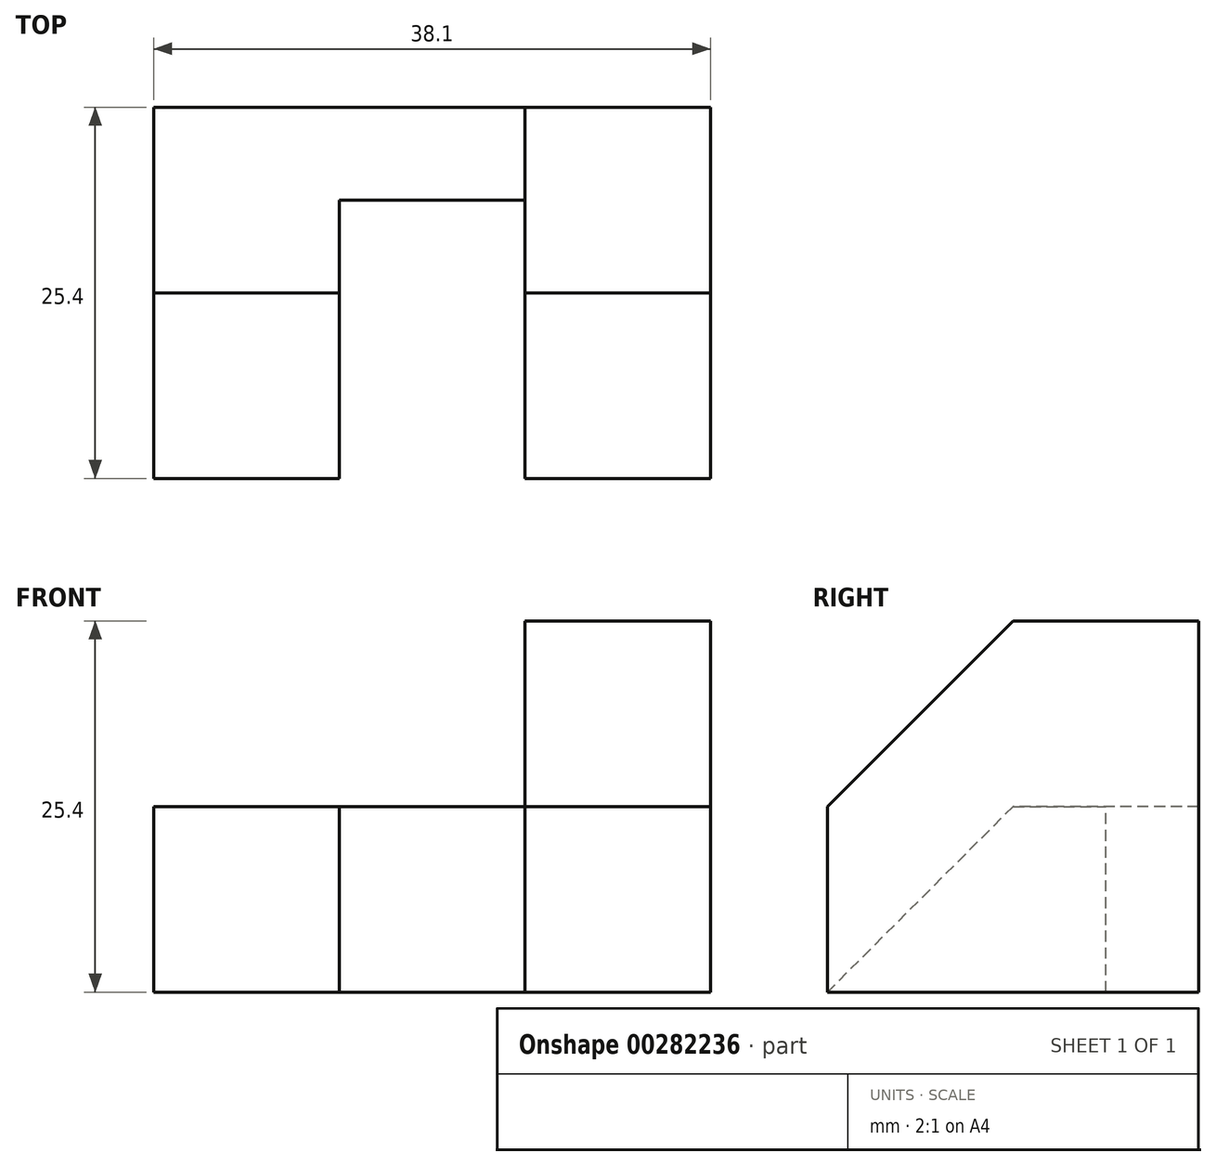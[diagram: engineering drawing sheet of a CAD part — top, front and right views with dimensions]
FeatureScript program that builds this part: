
annotation { "Feature Type Name" : "Feature", "Feature Type Description" : "" }
export const myFeature = defineFeature(function(context is Context, id is Id, definition is map)
    precondition{}
    {
        {
            var Q0;
            Q0=qCreatedBy(makeId("Right.planeOp"),FACE);
            var sketch = newSketch(context, id + "F0", { "sketchPlane" : qUnion([Q0])});
            skLineSegment(sketch, "E0.bottom", {"start": v(0, 0) * mm, "end": v(25.4, 0) * mm});
            skLineSegment(sketch, "E0.top", {"start": v(0, 25.4) * mm, "end": v(25.4, 25.4) * mm});
            skLineSegment(sketch, "E0.left", {"start": v(0, 0) * mm, "end": v(0, 25.4) * mm});
            skLineSegment(sketch, "E0.right", {"start": v(25.4, 0) * mm, "end": v(25.4, 25.4) * mm});
            skSolve(sketch);
        }
        {
            var Q0;
            Q0 = qSketchRegion(id + "F0", true);
            extrude(context, id + "F1", {"entities" : qUnion([Q0]), "depth" : 12.7 * mm});
        }
        {
            var Q0;
            Q0=makeQuery(id+"F1.opExtrude","CAP_FACE",FACE,{"disambiguationData":[OSD([sQuery(id+"F0.wireOp",EDGE,"E0.bottom"),sQuery(id+"F0.wireOp",EDGE,"E0.top"),sQuery(id+"F0.wireOp",EDGE,"E0.left"),sQuery(id+"F0.wireOp",EDGE,"E0.right")])],"isStart":false});
            var sketch = newSketch(context, id + "F2", { "sketchPlane" : qUnion([Q0])});
            skLineSegment(sketch, "E1", {"start": v(0, 25.4) * mm, "end": v(12.7, 25.4) * mm});
            skLineSegment(sketch, "E2", {"start": v(12.7, 25.4) * mm, "end": v(0, 12.7) * mm});
            skLineSegment(sketch, "E3", {"start": v(0, 12.7) * mm, "end": v(0, 25.4) * mm});
            skSolve(sketch);
        }
        {
            var Q0;
            Q0 = qSketchRegion(id + "F2", true);
            var Q1;
            Q1=makeQuery(id+"F2.imprint","IMPRINT",FACE,{"disambiguationData":[TD([[makeQuery(id+"F2.imprint","IMPRINT",EDGE,{"derivedFrom":sQuery(id+"F2.wireOp",EDGE,"E1")}),-1.0]])]});
            extrude(context, id + "F3", {"entities" : qUnion([Q0, Q1]), "operationType" : NewBodyOperationType.REMOVE, "oppositeDirection" : true, "depth" : 12.7 * mm});
        }
        {
            var Q0;
            Q0=makeQuery(id+"F1.opExtrude","CAP_FACE",FACE,{"disambiguationData":[OSD([sQuery(id+"F0.wireOp",EDGE,"E0.bottom"),sQuery(id+"F0.wireOp",EDGE,"E0.top"),sQuery(id+"F0.wireOp",EDGE,"E0.left"),sQuery(id+"F0.wireOp",EDGE,"E0.right")])],"isStart":true});
            var sketch = newSketch(context, id + "F4", { "sketchPlane" : qUnion([Q0])});
            skLineSegment(sketch, "E4.bottom", {"start": v(-25.4, 0) * mm, "end": v(-19.05, 0) * mm});
            skLineSegment(sketch, "E4.top", {"start": v(-25.4, 12.7) * mm, "end": v(-19.05, 12.7) * mm});
            skLineSegment(sketch, "E4.left", {"start": v(-25.4, 0) * mm, "end": v(-25.4, 12.7) * mm});
            skLineSegment(sketch, "E4.right", {"start": v(-19.05, 0) * mm, "end": v(-19.05, 12.7) * mm});
            skSolve(sketch);
        }
        {
            var Q0;
            Q0=makeQuery(id+"F4.imprint","IMPRINT",FACE,{"disambiguationData":[TD([[makeQuery(id+"F4.imprint","IMPRINT",EDGE,{"derivedFrom":sQuery(id+"F4.wireOp",EDGE,"E4.bottom")}),-1.0]])]});
            extrude(context, id + "F5", {"entities" : qUnion([Q0]), "operationType" : NewBodyOperationType.ADD, "depth" : 25.4 * mm});
        }
        {
            var Q0;
            Q0=makeQuery(id+"F5.opExtrude","SWEPT_FACE",FACE,{"disambiguationData":[OSD([sQuery(id+"F4.wireOp",EDGE,"E4.right")])]});
            var sketch = newSketch(context, id + "F6", { "sketchPlane" : qUnion([Q0])});
            skLineSegment(sketch, "E5.bottom", {"start": v(-25.4, 0) * mm, "end": v(-12.7, 0) * mm});
            skLineSegment(sketch, "E5.top", {"start": v(-25.4, 12.7) * mm, "end": v(-12.7, 12.7) * mm});
            skLineSegment(sketch, "E5.left", {"start": v(-25.4, 0) * mm, "end": v(-25.4, 12.7) * mm});
            skLineSegment(sketch, "E5.right", {"start": v(-12.7, 0) * mm, "end": v(-12.7, 12.7) * mm});
            skSolve(sketch);
        }
        {
            var Q0;
            Q0 = qSketchRegion(id + "F6", true);
            extrude(context, id + "F7", {"entities" : qUnion([Q0]), "operationType" : NewBodyOperationType.ADD, "depth" : 19.05 * mm});
        }
        {
            var Q0;
            Q0=makeQuery(id+"F7.opExtrude","SWEPT_FACE",FACE,{"disambiguationData":[OSD([sQuery(id+"F6.wireOp",EDGE,"E5.right")])]});
            var sketch = newSketch(context, id + "F8", { "sketchPlane" : qUnion([Q0])});
            skLineSegment(sketch, "E6", {"start": v(0, 0) * mm, "end": v(0, 12.7) * mm});
            skLineSegment(sketch, "E7", {"start": v(0, 12.7) * mm, "end": v(12.7, 12.7) * mm});
            skLineSegment(sketch, "E8", {"start": v(12.7, 12.7) * mm, "end": v(0, 0) * mm});
            skSolve(sketch);
        }
        {
            var Q0;
            Q0=makeQuery(id+"F8.imprint","IMPRINT",FACE,{"disambiguationData":[TD([[makeQuery(id+"F8.imprint","IMPRINT",EDGE,{"derivedFrom":sQuery(id+"F8.wireOp",EDGE,"E6")}),-1.0]])]});
            extrude(context, id + "F9", {"entities" : qUnion([Q0]), "operationType" : NewBodyOperationType.REMOVE, "oppositeDirection" : true, "depth" : 12.7 * mm});
        }
    });
